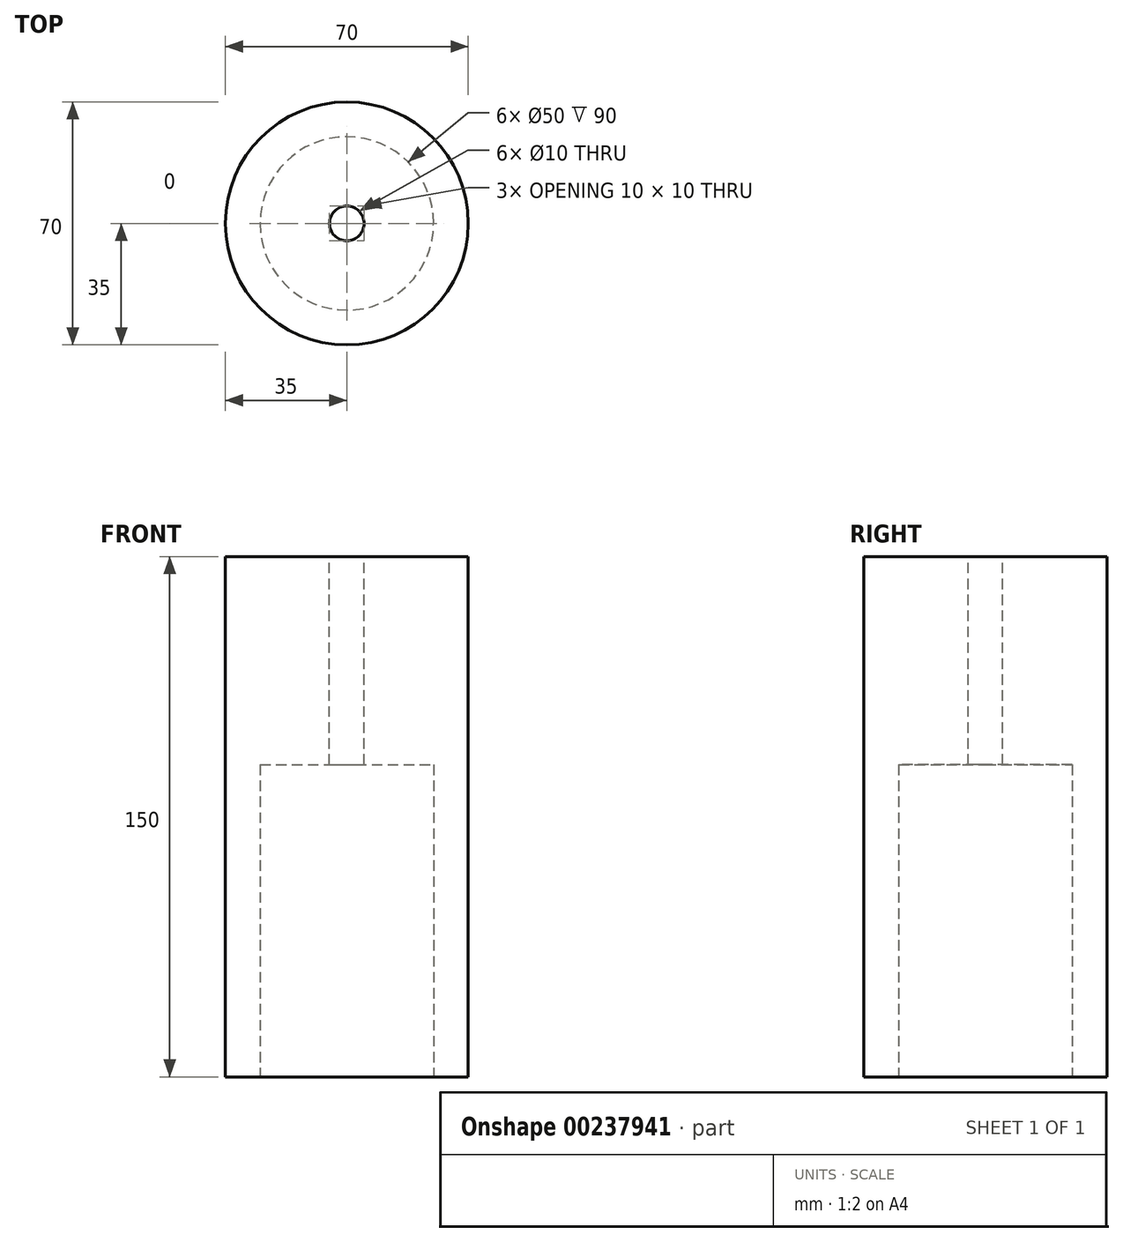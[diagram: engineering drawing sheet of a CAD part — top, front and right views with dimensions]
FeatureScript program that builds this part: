
annotation { "Feature Type Name" : "Feature", "Feature Type Description" : "" }
export const myFeature = defineFeature(function(context is Context, id is Id, definition is map)
    precondition{}
    {
        {
            var Q0;
            Q0=qCreatedBy(makeId("Top.planeOp"),FACE);
            var sketch = newSketch(context, id + "F0", { "sketchPlane" : qUnion([Q0])});
            skCircle(sketch, "E0", {"center": v(0, 0) * mm, "radius": 35 * mm});
            skSolve(sketch);
        }
        {
            var Q0;
            Q0 = qSketchRegion(id + "F0", true);
            extrude(context, id + "F1", {"entities" : qUnion([Q0]), "depth" : 150 * mm});
        }
        {
            var Q0;
            Q0=makeQuery(id+"F1.opExtrude","CAP_FACE",FACE,{"disambiguationData":[OSD([sQuery(id+"F0.wireOp",EDGE,"E0")])],"isStart":true});
            var sketch = newSketch(context, id + "F2", { "sketchPlane" : qUnion([Q0])});
            skCircle(sketch, "E1", {"center": v(0, 0) * mm, "radius": 25 * mm});
            skSolve(sketch);
        }
        {
            var Q0;
            Q0 = qSketchRegion(id + "F2", true);
            extrude(context, id + "F3", {"entities" : qUnion([Q0]), "operationType" : NewBodyOperationType.REMOVE, "oppositeDirection" : true, "depth" : 90 * mm});
        }
        {
            var Q0;
            Q0=makeQuery(id+"F1.opExtrude","CAP_FACE",FACE,{"disambiguationData":[OSD([sQuery(id+"F0.wireOp",EDGE,"E0")])],"isStart":false});
            var sketch = newSketch(context, id + "F4", { "sketchPlane" : qUnion([Q0])});
            skCircle(sketch, "E2", {"center": v(0, 0) * mm, "radius": 5 * mm});
            skSolve(sketch);
        }
        {
            var Q0;
            Q0 = qSketchRegion(id + "F4", true);
            extrude(context, id + "F5", {"entities" : qUnion([Q0]), "operationType" : NewBodyOperationType.REMOVE, "endBound" : BoundingType.THROUGH_ALL, "oppositeDirection" : true, "depth" : 25 * mm});
        }
    });
